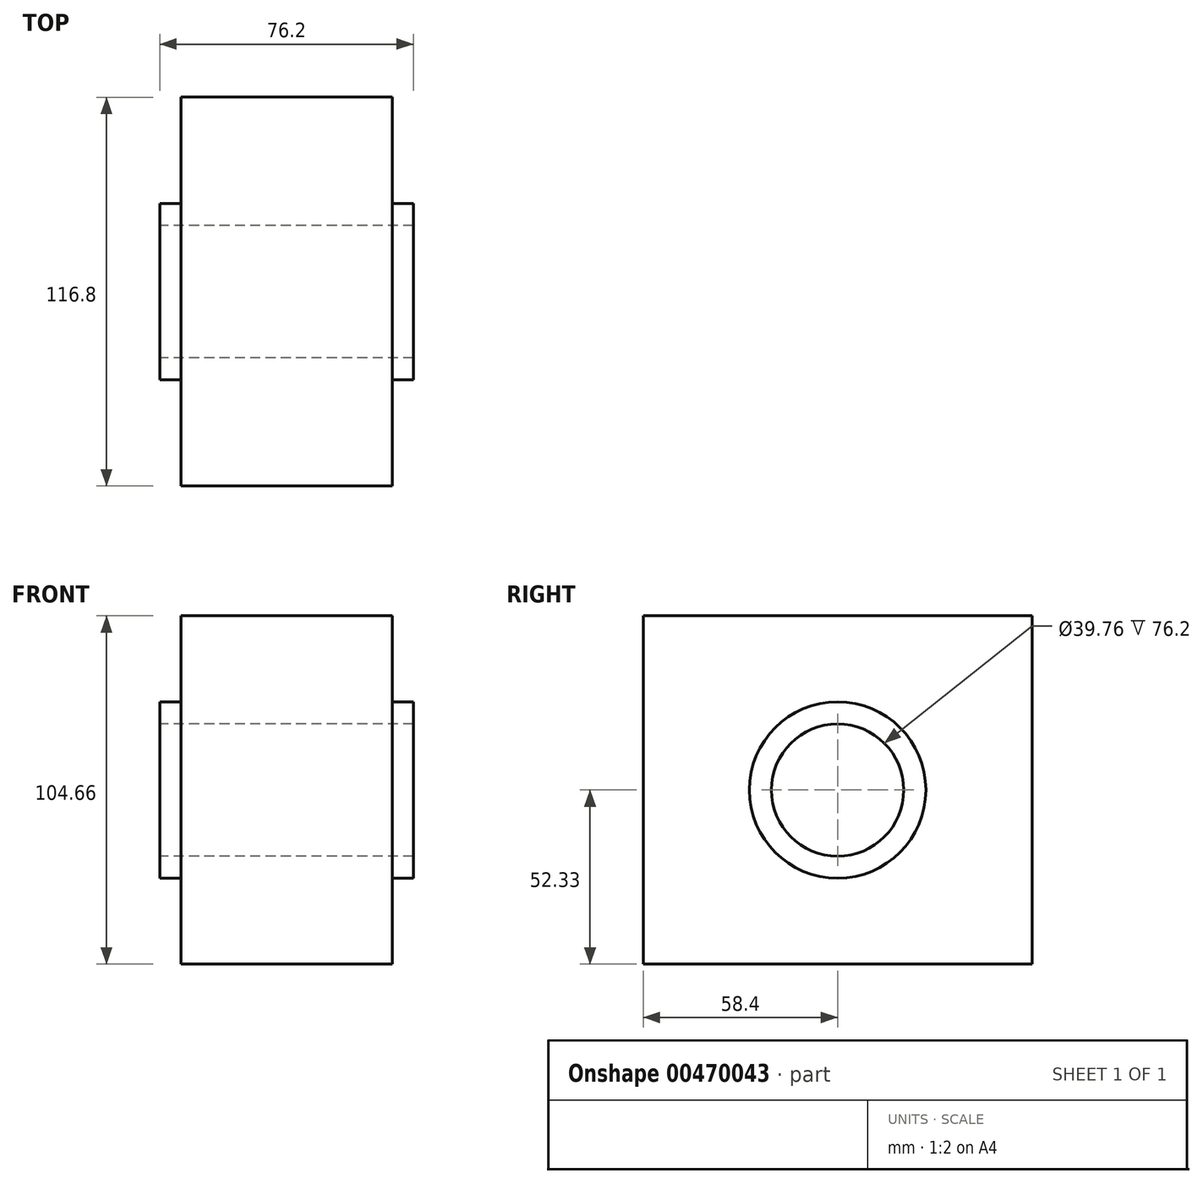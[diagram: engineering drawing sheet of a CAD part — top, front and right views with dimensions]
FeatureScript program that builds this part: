
annotation { "Feature Type Name" : "Feature", "Feature Type Description" : "" }
export const myFeature = defineFeature(function(context is Context, id is Id, definition is map)
    precondition{}
    {
        {
            var Q0;
            Q0=qCreatedBy(makeId("Right.planeOp"),FACE);
            var sketch = newSketch(context, id + "F0", { "sketchPlane" : qUnion([Q0])});
            skLineSegment(sketch, "E0.bottom", {"start": v(58.4, -52.33) * mm, "end": v(-58.4, -52.33) * mm});
            skLineSegment(sketch, "E0.top", {"start": v(58.4, 52.33) * mm, "end": v(-58.4, 52.33) * mm});
            skLineSegment(sketch, "E0.left", {"start": v(58.4, -52.33) * mm, "end": v(58.4, 52.33) * mm});
            skLineSegment(sketch, "E0.right", {"start": v(-58.4, -52.33) * mm, "end": v(-58.4, 52.33) * mm});
            skPoint(sketch, "E0.middle", {"position": v(0, 0) * mm});
            skCircle(sketch, "E1", {"center": v(0, 0) * mm, "radius": 26.52 * mm});
            skCircle(sketch, "E2", {"center": v(0, 0) * mm, "radius": 19.88 * mm});
            skSolve(sketch);
        }
        {
            var Q0;
            Q0=makeQuery(id+"F0.imprint","IMPRINT",FACE,{"disambiguationData":[TD([[makeQuery(id+"F0.imprint","IMPRINT",EDGE,{"derivedFrom":sQuery(id+"F0.wireOp",EDGE,"E0.bottom")}),-1.0]])]});
            extrude(context, id + "F1", {"entities" : qUnion([Q0]), "endBound" : BoundingType.SYMMETRIC, "depth" : 63.5 * mm});
        }
        {
            var Q0;
            Q0=makeQuery(id+"F0.imprint","IMPRINT",FACE,{"disambiguationData":[TD([[makeQuery(id+"F0.imprint","IMPRINT",EDGE,{"derivedFrom":sQuery(id+"F0.wireOp",EDGE,"E1")}),1.0]])]});
            extrude(context, id + "F2", {"entities" : qUnion([Q0]), "operationType" : NewBodyOperationType.ADD, "endBound" : BoundingType.SYMMETRIC, "depth" : 76.2 * mm});
        }
    });
